# Revit family: NBS_HeatraeSadia_InstntnsWtrHtrsPckgdPltHeatExchngrs_Hi-MaxInstantIDHeatInterfaceUnit
name_source: partatom
category: Plumbing Fixtures
revit_build: Autodesk Revit 2014 (Build: 20130709_2115(x64)
units: mm (PartAtom-declared; Revit-internal decimal feet)

## types (2) — shared parameters
Accessories = Central heating programmable room thermostat, Central heating zone valve, Concealed casing fixing screw, First fix rail, Heat meter, Insulated white powder coated steel casing, Stand-off assemblies, Tenants assembly
Arrangement = Instantaneous
AssetType = Fixed
CentralHeatingExpansionVesselVolume = 8 L
Connections = ¾" BSP female and 15 mm pipe
Description = Heat interface unit
DurationUnit = year
Features = Compact design, no need for boiler flues, suitable for single and dual zone heating systems, scale reducing feature
Fixing = Wall fixed
HeatInterfaceUnitMaterial = NBS_Concept
Height = 776 mm  [stored 2.54593 ft]
IfcExportAs = IfcBoilerType
IfcExportType = WATER
IsWaterStorageHeater = No
Length = 507 mm  [stored 1.66339 ft]
ManufacturerName = Heatrae Sadia
ManufacturerURL = www.heatraesadia.com
NBSCertification = http://www.nationalbimlibrary.com
NBSDescription = Instantaneous water heaters, packaged plate heat exchangers
NBSReference = 90-15-35/420
NominalHeight = 776 mm  [stored 2.54593 ft]
NominalLength = 507 mm  [stored 1.66339 ft]
NominalWidth = 279 mm
OutletTemperatureRange = 90
PackageUnit = Heat interface unit with two plate heat exchangers and PID controller
PressureRating = 3-10 bar
PrimaryMedium = Medium temperature hot water
ProductInformation = www.heatraesadia.com/docs/Heatrae_Sadia_Hi-Max_Instant_ID.pdf
SafetyFeatures = Safety tempering feature
SecondaryMedium = Water
Size = 776 x 507 x 279 mm
Uniclass2015Description = Instantaneous plate heat exchangers
Uniclass2015Reference = Pr_60_60_38_42
Uniclass2015Version = Products v1.1
Version = 1
WarrantyDurationUnit = year
WaterStorageCapacity = 0
Width = 279 mm
zero-valued in all types: CWFU, HWFU, HeatOutput, NominalEfficiency, NominalEnergyConsumption, NominalPartLoadRatio

## per-type parameters (varying)
| type | BIMObjectName | ModelNumber | ModelReference | Name | PrimaryFlowRate | Rating | Weight |
| ID-5/60 | NBS_HeatraeSadia_InstantaneousWaterHeatersPackagedPlateHeatExchangers_Hi-MaxInstantIDHeatInterfaceUnit-ID-5/60 | 95:050:202 | Hi-Max Instant ID Heat Interface Unit - ID-5/60 | InstantaneousWaterHeatersPackagedPlateHeatExchangers_Hi-MaxInstantIDHeatInterfaceUnit-ID-5/60_HeatraeSadia | DHW mode: 990 L/hour (maximum); Heating mode: 390 L/hour (maximum) | Heat exchanger: 10.43 kW; Unit: 62.5 kW (maximum) | 37.1 |
| ID-5/80 | NBS_HeatraeSadia_InstantaneousWaterHeatersPackagedPlateHeatExchangers_Hi-MaxInstantIDHeatInterfaceUnit-ID-5/80 | 95:050:203 | Hi-Max Instant ID Heat Interface Unit - ID-5/80 | InstantaneousWaterHeatersPackagedPlateHeatExchangers_Hi-MaxInstantIDHeatInterfaceUnit-ID-5/80_HeatraeSadia | DHW mode: 1330 L/hour (maximum); Heating mode: 480 L/hour (maximum) | Heat exchanger: 13.5 kW; Unit: 78.5 kW (maximum) | 37.3 |

note: [stored X ft] marks values corroborated as IEEE doubles in the binary element streams (Revit-internal decimal feet)

## geometry (parser evidence)
native form markers: Sweep x1
no freeform markers — native parametric forms only
